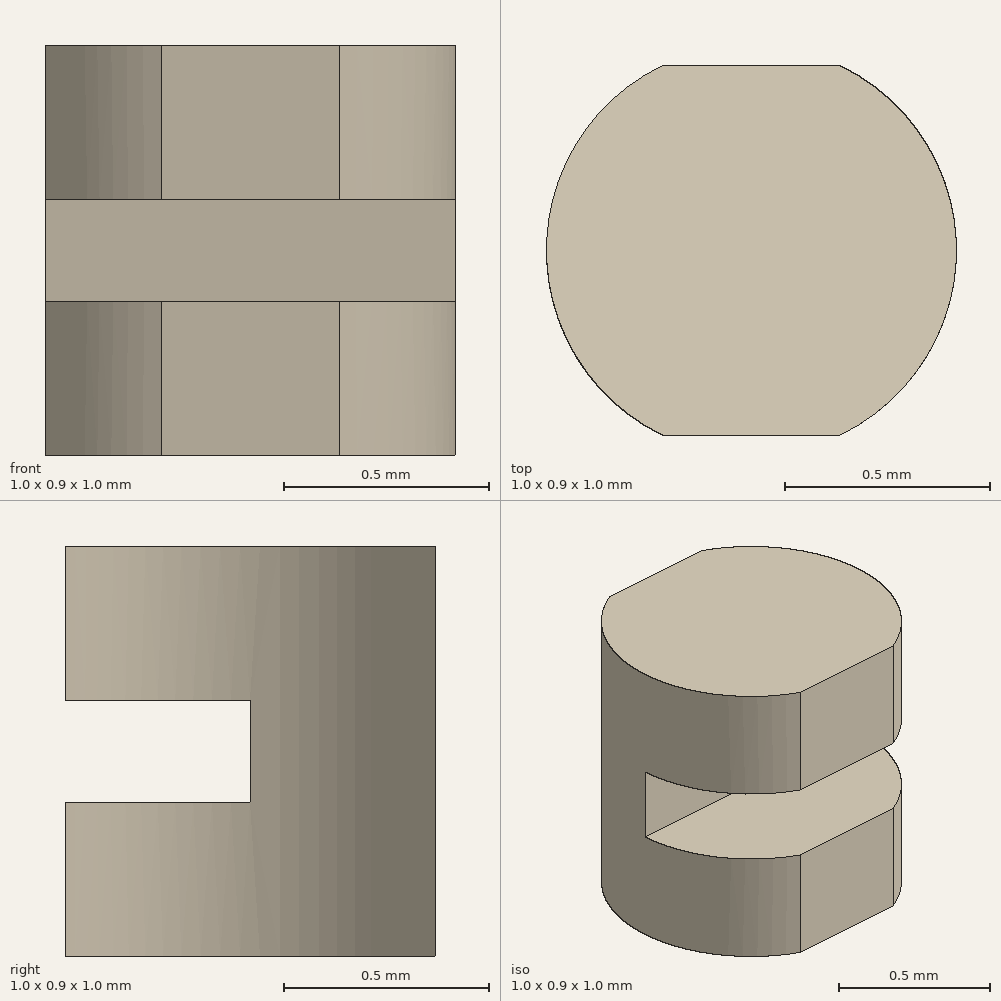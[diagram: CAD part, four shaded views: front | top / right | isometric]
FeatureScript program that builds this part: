
annotation { "Feature Type Name" : "Feature", "Feature Type Description" : "" }
export const myFeature = defineFeature(function(context is Context, id is Id, definition is map)
    precondition{}
    {
        {
            var Q0;
            Q0=qCreatedBy(makeId("Top.planeOp"),FACE);
            var sketch = newSketch(context, id + "F0", { "sketchPlane" : qUnion([Q0])});
            skCircle(sketch, "E0", {"center": v(0, 0) * mm, "radius": 0.5 * mm});
            skSolve(sketch);
        }
        {
            var Q0;
            Q0=makeQuery(id+"F0.imprint","IMPRINT",FACE,{"disambiguationData":[TD([[makeQuery(id+"F0.imprint","IMPRINT",EDGE,{"derivedFrom":sQuery(id+"F0.wireOp",EDGE,"E0")}),1.0]])]});
            extrude(context, id + "F1", {"entities" : qUnion([Q0]), "endBound" : BoundingType.SYMMETRIC, "depth" : 1 * mm, "offsetDistance" : 25 * mm});
        }
        {
            var Q0;
            Q0=qCreatedBy(makeId("Right.planeOp"),FACE);
            var sketch = newSketch(context, id + "F2", { "sketchPlane" : qUnion([Q0])});
            skLineSegment(sketch, "E1.bottom", {"start": v(0, 0.13) * mm, "end": v(-1, 0.12) * mm});
            skLineSegment(sketch, "E1.top", {"start": v(0, -0.13) * mm, "end": v(-1, -0.13) * mm});
            skLineSegment(sketch, "E1.left", {"start": v(0, 0.12) * mm, "end": v(0, -0.12) * mm});
            skLineSegment(sketch, "E1.right", {"start": v(-1, 0.12) * mm, "end": v(-1, -0.13) * mm});
            skSolve(sketch);
        }
        {
            var Q0;
            Q0=makeQuery(id+"F2.imprint","IMPRINT",FACE,{"disambiguationData":[TD([[makeQuery(id+"F2.imprint","IMPRINT",EDGE,{"derivedFrom":sQuery(id+"F2.wireOp",EDGE,"E1.bottom")}),1.0]])]});
            extrude(context, id + "F3", {"entities" : qUnion([Q0]), "operationType" : NewBodyOperationType.REMOVE, "endBound" : BoundingType.SYMMETRIC, "oppositeDirection" : true, "depth" : 25 * mm, "offsetDistance" : 25 * mm});
        }
        {
            var Q0;
            Q0=qCreatedBy(makeId("Right.planeOp"),FACE);
            var sketch = newSketch(context, id + "F4", { "sketchPlane" : qUnion([Q0])});
            skLineSegment(sketch, "E2.bottom", {"start": v(0.45, 0.58) * mm, "end": v(1.15, 0.58) * mm});
            skLineSegment(sketch, "E2.top", {"start": v(0.45, -0.6) * mm, "end": v(1.15, -0.6) * mm});
            skLineSegment(sketch, "E2.left", {"start": v(0.45, 0.58) * mm, "end": v(0.45, -0.6) * mm});
            skLineSegment(sketch, "E2.right", {"start": v(1.15, 0.58) * mm, "end": v(1.15, -0.6) * mm});
            skLineSegment(sketch, "E3.bottom", {"start": v(-0.99, 0.72) * mm, "end": v(-0.45, 0.72) * mm});
            skLineSegment(sketch, "E3.top", {"start": v(-0.99, -0.7) * mm, "end": v(-0.45, -0.7) * mm});
            skLineSegment(sketch, "E3.left", {"start": v(-0.99, 0.72) * mm, "end": v(-0.99, -0.7) * mm});
            skLineSegment(sketch, "E3.right", {"start": v(-0.45, 0.72) * mm, "end": v(-0.45, -0.7) * mm});
            skSolve(sketch);
        }
        {
            var Q0;
            Q0=makeQuery(id+"F4.imprint","IMPRINT",FACE,{"disambiguationData":[TD([[makeQuery(id+"F4.imprint","IMPRINT",EDGE,{"derivedFrom":sQuery(id+"F4.wireOp",EDGE,"E2.bottom")}),-1.0]])]});
            var Q1;
            Q1=makeQuery(id+"F4.imprint","IMPRINT",FACE,{"disambiguationData":[TD([[makeQuery(id+"F4.imprint","IMPRINT",EDGE,{"derivedFrom":sQuery(id+"F4.wireOp",EDGE,"E3.bottom")}),-1.0]])]});
            extrude(context, id + "F5", {"entities" : qUnion([Q0, Q1]), "operationType" : NewBodyOperationType.REMOVE, "endBound" : BoundingType.SYMMETRIC, "oppositeDirection" : true, "depth" : 25 * mm, "offsetDistance" : 25 * mm});
        }
    });
